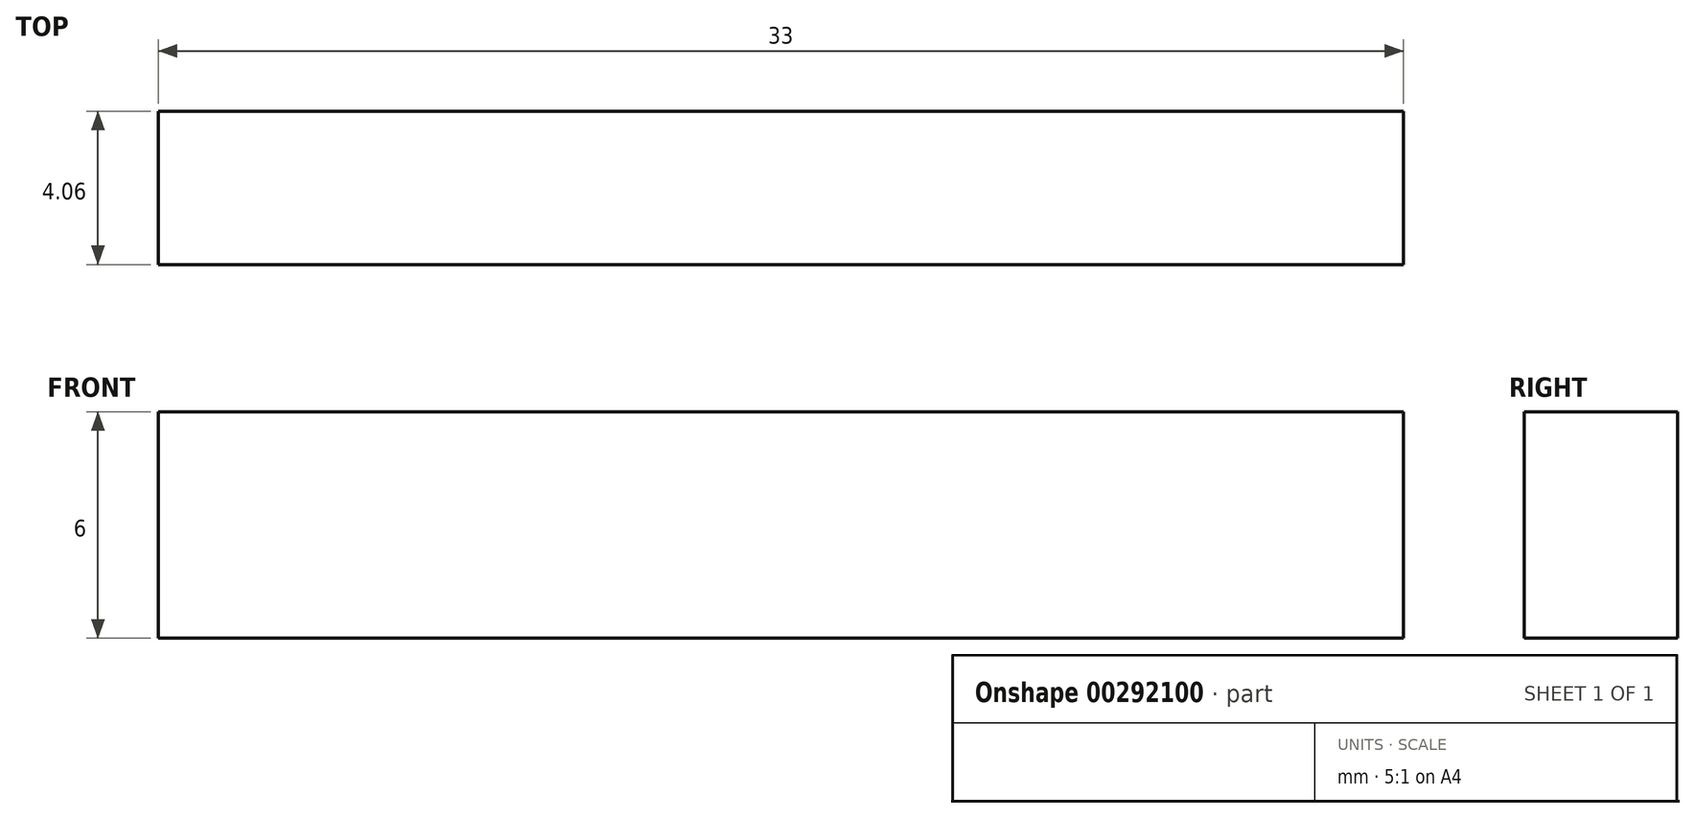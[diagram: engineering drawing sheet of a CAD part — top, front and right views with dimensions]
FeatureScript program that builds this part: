
annotation { "Feature Type Name" : "Feature", "Feature Type Description" : "" }
export const myFeature = defineFeature(function(context is Context, id is Id, definition is map)
    precondition{}
    {
        {
            var Q0;
            Q0=qCreatedBy(makeId("Front.planeOp"),FACE);
            var sketch = newSketch(context, id + "F0", { "sketchPlane" : qUnion([Q0])});
            skLineSegment(sketch, "E0.bottom", {"start": v(-12.83, 6) * mm, "end": v(20.17, 6) * mm});
            skLineSegment(sketch, "E0.top", {"start": v(-12.83, 0) * mm, "end": v(20.17, 0) * mm});
            skLineSegment(sketch, "E0.left", {"start": v(-12.83, 6) * mm, "end": v(-12.83, 0) * mm});
            skLineSegment(sketch, "E0.right", {"start": v(20.17, 6) * mm, "end": v(20.17, 0) * mm});
            skSolve(sketch);
        }
        {
            var Q0;
            Q0=makeQuery(id+"F0.imprint","IMPRINT",FACE,{"disambiguationData":[TD([[makeQuery(id+"F0.imprint","IMPRINT",EDGE,{"derivedFrom":sQuery(id+"F0.wireOp",EDGE,"E0.bottom")}),-1.0]])]});
            extrude(context, id + "F1", {"entities" : qUnion([Q0]), "endBound" : BoundingType.SYMMETRIC, "depth" : 4.06 * mm});
        }
    });
